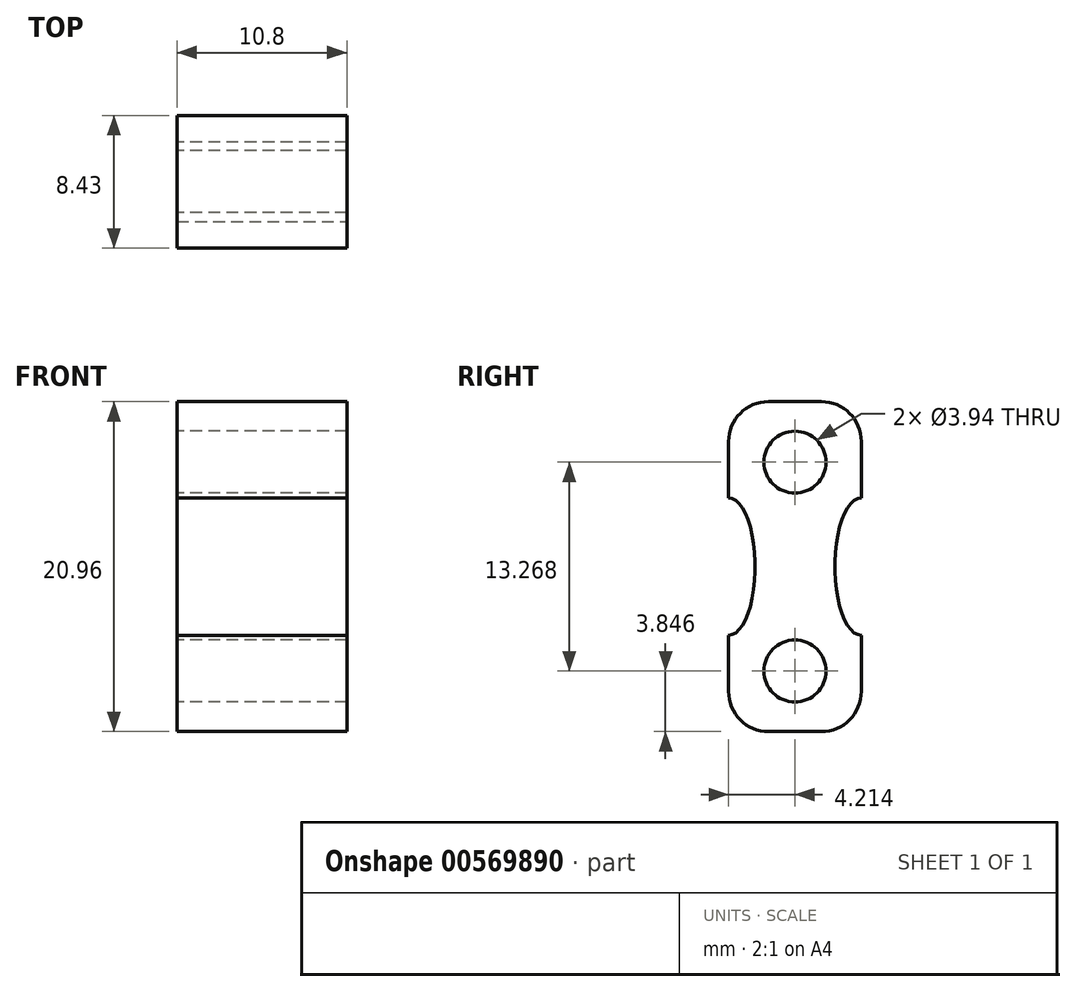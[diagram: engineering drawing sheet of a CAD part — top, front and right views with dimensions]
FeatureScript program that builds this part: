
annotation { "Feature Type Name" : "Feature", "Feature Type Description" : "" }
export const myFeature = defineFeature(function(context is Context, id is Id, definition is map)
    precondition{}
    {
        {
            var Q0;
            Q0=qCreatedBy(makeId("Front.planeOp"),FACE);
            var sketch = newSketch(context, id + "F0", { "sketchPlane" : qUnion([Q0])});
            skLineSegment(sketch, "E0.bottom", {"start": v(-5.4, 10.48) * mm, "end": v(5.4, 10.48) * mm});
            skLineSegment(sketch, "E0.top", {"start": v(-5.4, -10.48) * mm, "end": v(5.4, -10.48) * mm});
            skLineSegment(sketch, "E0.left", {"start": v(-5.4, 10.48) * mm, "end": v(-5.4, -10.48) * mm});
            skLineSegment(sketch, "E0.right", {"start": v(5.4, 10.48) * mm, "end": v(5.4, -10.48) * mm});
            skPoint(sketch, "E0.middle", {"position": v(0, 0) * mm});
            skSolve(sketch);
        }
        {
            var Q0;
            Q0=makeQuery(id+"F0.imprint","IMPRINT",FACE,{"disambiguationData":[TD([[makeQuery(id+"F0.imprint","IMPRINT",EDGE,{"derivedFrom":sQuery(id+"F0.wireOp",EDGE,"E0.bottom")}),-1.0]])]});
            extrude(context, id + "F1", {"entities" : qUnion([Q0]), "depth" : 8.43 * mm, "offsetDistance" : 25.4 * mm});
        }
        {
            var Q0;
            Q0=makeQuery(id+"F1.opExtrude","SWEPT_FACE",FACE,{"disambiguationData":[OSD([sQuery(id+"F0.wireOp",EDGE,"E0.left")])]});
            var sketch = newSketch(context, id + "F2", { "sketchPlane" : qUnion([Q0])});
            skCircle(sketch, "E1", {"center": v(4.22, 6.63) * mm, "radius": 1.97 * mm});
            skCircle(sketch, "E2.MirrorC", {"center": v(4.22, -6.63) * mm, "radius": 1.97 * mm});
            skSolve(sketch);
        }
        {
            var Q0;
            Q0=makeQuery(id+"F2.imprint","IMPRINT",FACE,{"disambiguationData":[TD([[makeQuery(id+"F2.imprint","IMPRINT",EDGE,{"derivedFrom":sQuery(id+"F2.wireOp",EDGE,"E1")}),1.0]])]});
            var Q1;
            Q1=sQuery(id+"F2.wireOp",EDGE,"E1");
            extrude(context, id + "F3", {"entities" : qUnion([Q0]), "operationType" : NewBodyOperationType.REMOVE, "surfaceEntities" : qUnion([Q1]), "oppositeDirection" : true, "depth" : 26.92 * mm, "offsetDistance" : 25.4 * mm});
        }
        {
            var Q0;
            Q0 = qSketchRegion(id + "F2", true);
            extrude(context, id + "F4", {"entities" : qUnion([Q0]), "operationType" : NewBodyOperationType.REMOVE, "oppositeDirection" : true, "depth" : 25.4 * mm, "offsetDistance" : 25.4 * mm});
        }
        {
            var Q0;
            Q0=makeQuery(id+"F1.opExtrude","CAP_EDGE",EDGE,{"disambiguationData":[OSD([sQuery(id+"F0.wireOp",EDGE,"E0.bottom")])],"isStart":true});
            var Q1;
            Q1=makeQuery(id+"F1.opExtrude","CAP_EDGE",EDGE,{"disambiguationData":[OSD([sQuery(id+"F0.wireOp",EDGE,"E0.bottom")])],"isStart":false});
            var Q2;
            Q2=makeQuery(id+"F1.opExtrude","CAP_EDGE",EDGE,{"disambiguationData":[OSD([sQuery(id+"F0.wireOp",EDGE,"E0.top")])],"isStart":true});
            var Q3;
            Q3=makeQuery(id+"F1.opExtrude","CAP_EDGE",EDGE,{"disambiguationData":[OSD([sQuery(id+"F0.wireOp",EDGE,"E0.top")])],"isStart":false});
            fillet(context, id + "F5", {"entities" : qUnion([Q0, Q1, Q2, Q3]), "radius" : 2.54 * mm, "tangentPropagation" : true, "allowEdgeOverflow" : false});
        }
        {
            var Q0;
            Q0=qCreatedBy(makeId("Right.planeOp"),FACE);
            var sketch = newSketch(context, id + "F6", { "sketchPlane" : qUnion([Q0])});
            skEllipse(sketch, "E3", {"center": v(0, 0) * mm, "majorRadius": 4.36 * mm, "minorRadius": 1.69 * mm, "majorAxis": v(0, 1)});
            skLineSegment(sketch, "E4", {"start": v(-4.21, 6.64) * mm, "end": v(-4.21, 1.44) * mm, "construction": true});
            skEllipse(sketch, "E5.MirrorC", {"center": v(-8.43, 0) * mm, "majorRadius": 4.36 * mm, "minorRadius": 1.69 * mm, "majorAxis": v(0, 1)});
            skSolve(sketch);
        }
        {
            var Q0;
            Q0 = qSketchRegion(id + "F6", true);
            extrude(context, id + "F7", {"entities" : qUnion([Q0]), "operationType" : NewBodyOperationType.REMOVE, "oppositeDirection" : true, "depth" : 25.4 * mm, "offsetDistance" : 25.4 * mm, "hasSecondDirection" : true, "secondDirectionOppositeDirection" : false, "secondDirectionDepth" : 25.4 * mm});
        }
    });
